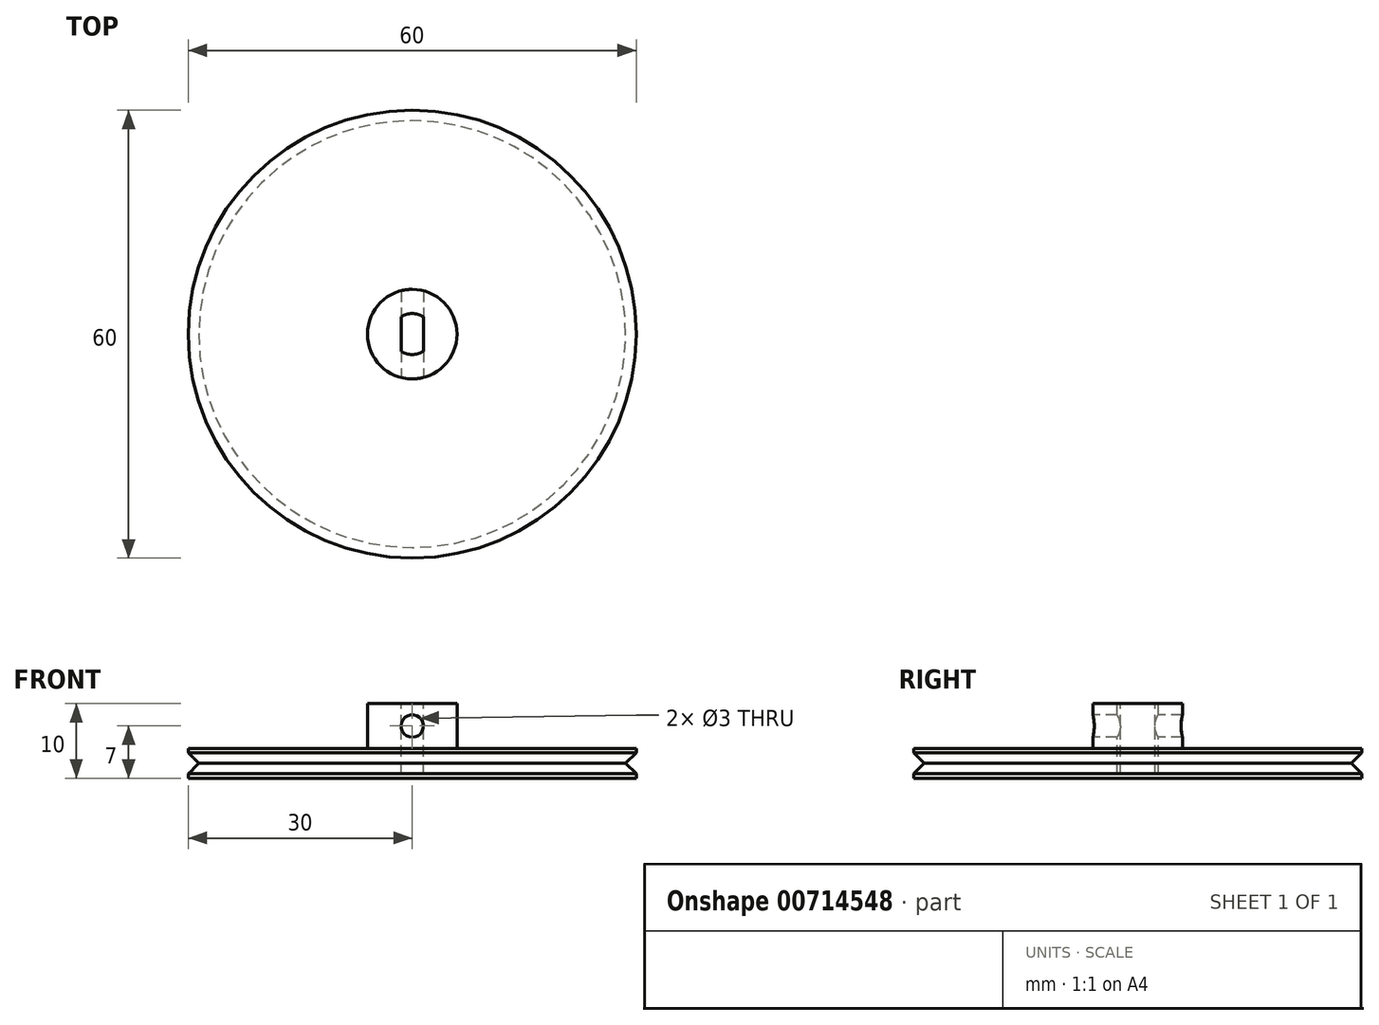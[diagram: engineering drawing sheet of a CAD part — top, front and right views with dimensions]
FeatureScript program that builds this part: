
annotation { "Feature Type Name" : "Feature", "Feature Type Description" : "" }
export const myFeature = defineFeature(function(context is Context, id is Id, definition is map)
    precondition{}
    {
        {
            var Q0;
            Q0=qCreatedBy(makeId("Top.planeOp"),FACE);
            var sketch = newSketch(context, id + "F0", { "sketchPlane" : qUnion([Q0])});
            skCircle(sketch, "E0", {"center": v(0, 0) * mm, "radius": 30 * mm});
            skCircle(sketch, "E1", {"center": v(0, 0) * mm, "radius": 6 * mm});
            skSolve(sketch);
        }
        {
            var Q0;
            Q0=makeQuery(id+"F0.imprint","IMPRINT",FACE,{"disambiguationData":[TD([[makeQuery(id+"F0.imprint","IMPRINT",EDGE,{"derivedFrom":sQuery(id+"F0.wireOp",EDGE,"E1")}),1.0]])]});
            var Q1;
            Q1=makeQuery(id+"F0.imprint","IMPRINT",FACE,{"disambiguationData":[TD([[makeQuery(id+"F0.imprint","IMPRINT",EDGE,{"derivedFrom":sQuery(id+"F0.wireOp",EDGE,"E0")}),1.0]])]});
            extrude(context, id + "F1", {"entities" : qUnion([Q0, Q1]), "oppositeDirection" : true, "depth" : 4 * mm, "offsetDistance" : 25 * mm});
        }
        {
            var Q0;
            Q0=makeQuery(id+"F0.imprint","IMPRINT",FACE,{"disambiguationData":[TD([[makeQuery(id+"F0.imprint","IMPRINT",EDGE,{"derivedFrom":sQuery(id+"F0.wireOp",EDGE,"E1")}),1.0]])]});
            extrude(context, id + "F2", {"entities" : qUnion([Q0]), "operationType" : NewBodyOperationType.ADD, "depth" : 6 * mm, "offsetDistance" : 25 * mm});
        }
        {
            var Q0;
            Q0=qCreatedBy(makeId("Front.planeOp"),FACE);
            var sketch = newSketch(context, id + "F3", { "sketchPlane" : qUnion([Q0])});
            skCircle(sketch, "E2", {"center": v(0, 3) * mm, "radius": 1.5 * mm});
            skSolve(sketch);
        }
        {
            var Q0;
            Q0 = qSketchRegion(id + "F3", true);
            extrude(context, id + "F4", {"entities" : qUnion([Q0]), "operationType" : NewBodyOperationType.REMOVE, "endBound" : BoundingType.SYMMETRIC, "oppositeDirection" : true, "depth" : 25 * mm, "offsetDistance" : 25 * mm});
        }
        {
            var Q0;
            Q0=makeQuery(id+"F2.opExtrude","CAP_FACE",FACE,{"disambiguationData":[OSD([sQuery(id+"F0.wireOp",EDGE,"E1")])],"isStart":false});
            var sketch = newSketch(context, id + "F5", { "sketchPlane" : qUnion([Q0])});
            skLineSegment(sketch, "E3.bottom", {"start": v(1.5, -2.3) * mm, "end": v(-1.5, -2.3) * mm});
            skLineSegment(sketch, "E3.top", {"start": v(1.5, 2.3) * mm, "end": v(-1.5, 2.3) * mm});
            skLineSegment(sketch, "E3.left", {"start": v(1.5, -2.3) * mm, "end": v(1.5, 2.3) * mm});
            skLineSegment(sketch, "E3.right", {"start": v(-1.5, -2.3) * mm, "end": v(-1.5, 2.3) * mm});
            skPoint(sketch, "E3.middle", {"position": v(0, 0) * mm});
            skArc(sketch, "E4", {"start": v(1.5, 2.3) * mm, "mid": v(0, 2.75) * mm, "end": v(-1.5, 2.3) * mm});
            skArc(sketch, "E5", {"start": v(-1.5, -2.3) * mm, "mid": v(0, -2.75) * mm, "end": v(1.5, -2.3) * mm});
            skSolve(sketch);
        }
        {
            var Q0;
            Q0=makeQuery(id+"F5.imprint","IMPRINT",FACE,{"disambiguationData":[TD([[makeQuery(id+"F5.imprint","IMPRINT",EDGE,{"derivedFrom":sQuery(id+"F5.wireOp",EDGE,"E3.bottom")}),-1.0]])]});
            var Q1;
            Q1=makeQuery(id+"F5.imprint","IMPRINT",FACE,{"disambiguationData":[TD([[makeQuery(id+"F5.imprint","IMPRINT",EDGE,{"derivedFrom":sQuery(id+"F5.wireOp",EDGE,"E3.top")}),-1.0]])]});
            var Q2;
            Q2=makeQuery(id+"F5.imprint","IMPRINT",FACE,{"disambiguationData":[TD([[makeQuery(id+"F5.imprint","IMPRINT",EDGE,{"derivedFrom":sQuery(id+"F5.wireOp",EDGE,"E3.bottom")}),1.0]])]});
            extrude(context, id + "F6", {"entities" : qUnion([Q0, Q1, Q2]), "operationType" : NewBodyOperationType.REMOVE, "oppositeDirection" : true, "depth" : 9.4 * mm, "offsetDistance" : 25 * mm});
        }
        {
            var Q0;
            Q0=qCreatedBy(makeId("Front.planeOp"),FACE);
            var sketch = newSketch(context, id + "F7", { "sketchPlane" : qUnion([Q0])});
            skLineSegment(sketch, "E6", {"start": v(-30, -4) * mm, "end": v(-30, 0) * mm, "construction": true});
            skLineSegment(sketch, "E7", {"start": v(-30, -0.59) * mm, "end": v(-28.59, -2) * mm});
            skLineSegment(sketch, "E8", {"start": v(-28.59, -2) * mm, "end": v(-30, -3.41) * mm});
            skLineSegment(sketch, "E9", {"start": v(-30, -2) * mm, "end": v(-25.87, -2) * mm, "construction": true});
            skLineSegment(sketch, "E10", {"start": v(0, 9.1) * mm, "end": v(0, -8.57) * mm, "construction": true});
            skLineSegment(sketch, "E11", {"start": v(-30, -0.59) * mm, "end": v(-30, -3.41) * mm});
            skSolve(sketch);
        }
        {
            var Q0;
            Q0 = qSketchRegion(id + "F7", true);
            var Q1;
            Q1=sQuery(id+"F7.wireOp",EDGE,"E10");
            revolve(context, id + "F8", {"operationType" : NewBodyOperationType.REMOVE, "surfaceOperationType" : NewSurfaceOperationType.NEW, "entities" : qUnion([Q0]), "axis" : qUnion([Q1]), "revolveType" : RevolveType.FULL, "oppositeDirection" : true});
        }
    });
